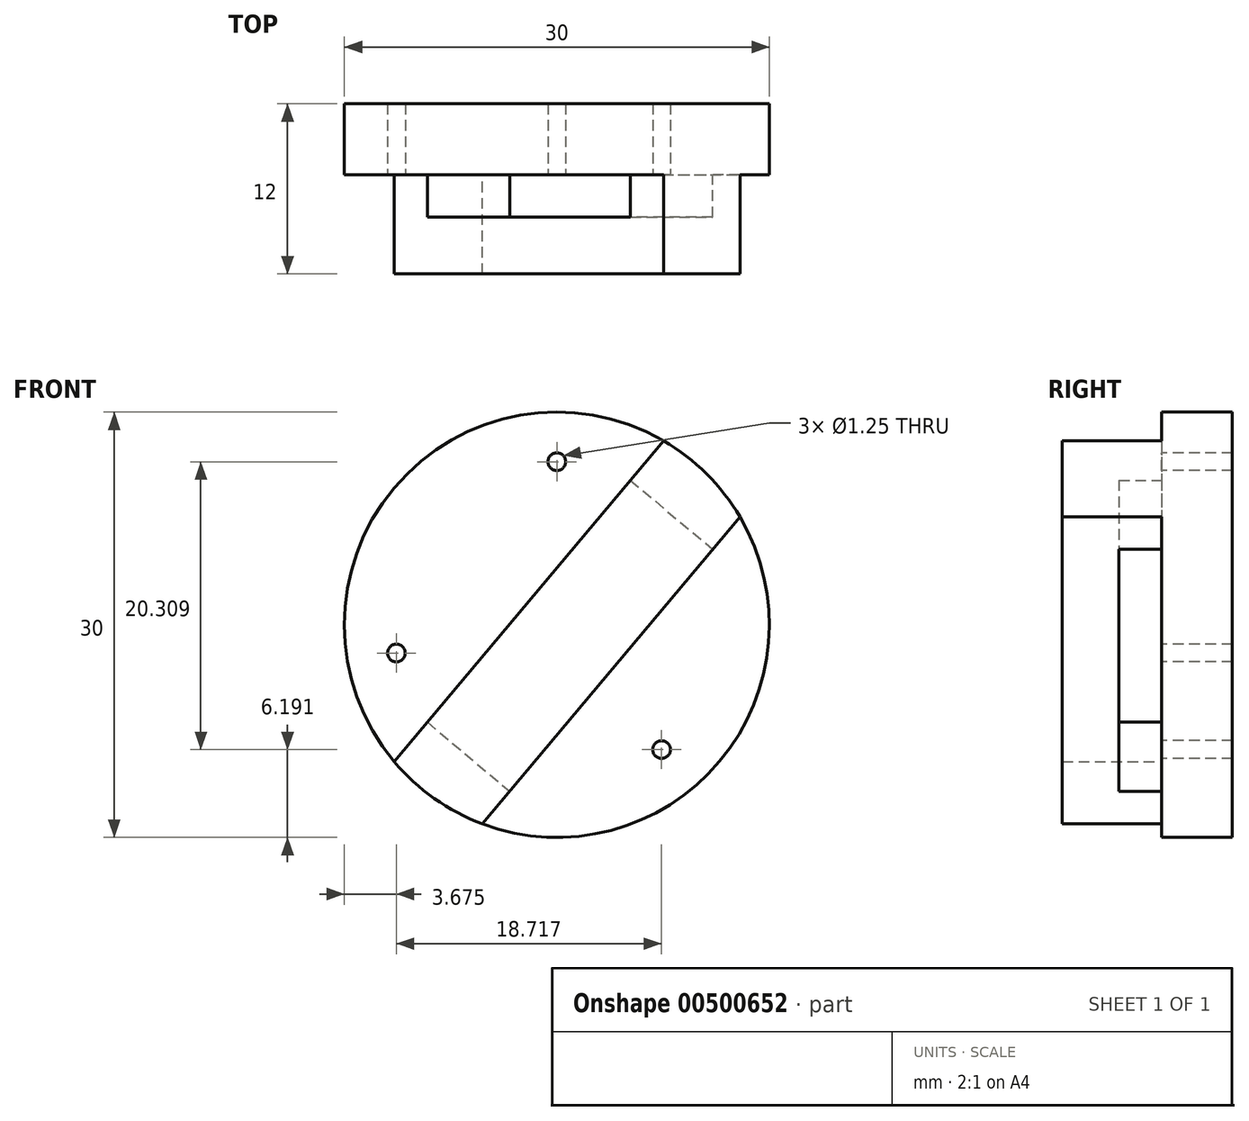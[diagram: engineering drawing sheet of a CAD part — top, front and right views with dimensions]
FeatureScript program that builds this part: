
annotation { "Feature Type Name" : "Feature", "Feature Type Description" : "" }
export const myFeature = defineFeature(function(context is Context, id is Id, definition is map)
    precondition{}
    {
        {
            var Q0;
            Q0=qCreatedBy(makeId("Front.planeOp"),FACE);
            var sketch = newSketch(context, id + "F0", { "sketchPlane" : qUnion([Q0])});
            skCircle(sketch, "E0", {"center": v(0, 0) * mm, "radius": 15 * mm});
            skLineSegment(sketch, "E1", {"start": v(0, 0) * mm, "end": v(0, 15) * mm});
            skLineSegment(sketch, "E2", {"start": v(0, 0) * mm, "end": v(-14.77, -2.6) * mm});
            skLineSegment(sketch, "E3", {"start": v(0, 0) * mm, "end": v(9.64, -11.5) * mm});
            skPoint(sketch, "E4", {"position": v(0, 11.5) * mm});
            skPoint(sketch, "E5", {"position": v(7.4, -8.8) * mm});
            skPoint(sketch, "E6", {"position": v(-11.33, -2) * mm});
            skLineSegment(sketch, "E7", {"start": v(7.53, 12.97) * mm, "end": v(0, 4) * mm});
            skLineSegment(sketch, "E8", {"start": v(0, 4) * mm, "end": v(-3.94, -0.7) * mm});
            skLineSegment(sketch, "E9", {"start": v(-3.94, -0.7) * mm, "end": v(-11.47, -9.67) * mm});
            skLineSegment(sketch, "E10", {"start": v(12.92, 7.62) * mm, "end": v(-5.26, -14.05) * mm});
            skLineSegment(sketch, "E11", {"start": v(5.2, 10.19) * mm, "end": v(11, 5.32) * mm});
            skLineSegment(sketch, "E12", {"start": v(-9.13, -6.88) * mm, "end": v(-3.33, -11.75) * mm});
            skSolve(sketch);
        }
        {
            var Q0;
            {var subQ0=sQuery(id+"F0.wireOp",EDGE,"E7");Q0=makeQuery(id+"F0.imprint","IMPRINT",FACE,{"disambiguationData":[TD([[makeQuery(id+"F0.imprint","IMPRINT",EDGE,{"derivedFrom":subQ0}),1.0]])]});}
            var Q1;
            {var subQ3=sQuery(id+"F0.wireOp",EDGE,"E8");Q1=makeQuery(id+"F0.imprint","IMPRINT",FACE,{"disambiguationData":[TD([[makeQuery(id+"F0.imprint","IMPRINT",EDGE,{"derivedFrom":subQ3}),1.0]])]});}
            var Q2;
            {var subQ0=sQuery(id+"F0.wireOp",EDGE,"E9");Q2=makeQuery(id+"F0.imprint","IMPRINT",FACE,{"disambiguationData":[TD([[makeQuery(id+"F0.imprint","IMPRINT",EDGE,{"derivedFrom":subQ0}),1.0]])]});}
            var Q3;
            {var subQ0=sQuery(id+"F0.wireOp",EDGE,"E12");Q3=makeQuery(id+"F0.imprint","IMPRINT",FACE,{"disambiguationData":[TD([[makeQuery(id+"F0.imprint","IMPRINT",EDGE,{"derivedFrom":subQ0}),1.0]])]});}
            var Q4;
            {var subQ0=sQuery(id+"F0.wireOp",EDGE,"E11");Q4=makeQuery(id+"F0.imprint","IMPRINT",FACE,{"disambiguationData":[TD([[makeQuery(id+"F0.imprint","IMPRINT",EDGE,{"derivedFrom":subQ0}),-1.0]])]});}
            extrude(context, id + "F1", {"entities" : qUnion([Q0, Q1, Q2, Q3, Q4]), "depth" : 12 * mm, "offsetDistance" : 25 * mm});
        }
        {
            var Q0;
            {var subQ3=sQuery(id+"F0.wireOp",EDGE,"E8");Q0=makeQuery(id+"F0.imprint","IMPRINT",FACE,{"disambiguationData":[TD([[makeQuery(id+"F0.imprint","IMPRINT",EDGE,{"derivedFrom":subQ3}),1.0]])]});}
            var Q1;
            {var subQ0=sQuery(id+"F0.wireOp",EDGE,"E11");Q1=makeQuery(id+"F0.imprint","IMPRINT",FACE,{"disambiguationData":[TD([[makeQuery(id+"F0.imprint","IMPRINT",EDGE,{"derivedFrom":subQ0}),-1.0]])]});}
            var Q2;
            {var subQ0=sQuery(id+"F0.wireOp",EDGE,"E12");Q2=makeQuery(id+"F0.imprint","IMPRINT",FACE,{"disambiguationData":[TD([[makeQuery(id+"F0.imprint","IMPRINT",EDGE,{"derivedFrom":subQ0}),1.0]])]});}
            extrude(context, id + "F2", {"entities" : qUnion([Q0, Q1, Q2]), "operationType" : NewBodyOperationType.REMOVE, "depth" : 8 * mm, "offsetDistance" : 25 * mm});
        }
        {
            var Q0;
            {var subQ0=sQuery(id+"F0.wireOp",EDGE,"E1");var subQ1=sQuery(id+"F0.wireOp",EDGE,"E0");var subQ2=makeQuery(id+"F0.imprint","INTERSECT",VERTEX,{"derivedFrom":[subQ1,subQ0]});Q0=makeQuery(id+"F0.imprint","IMPRINT",FACE,{"disambiguationData":[TD([[makeQuery(id+"F0.imprint","IMPRINT",EDGE,{"disambiguationData":[TD([[subQ2,1.0]])],"derivedFrom":subQ1}),1.0]])]});}
            var Q1;
            {var subQ0=sQuery(id+"F0.wireOp",EDGE,"E11");Q1=makeQuery(id+"F0.imprint","IMPRINT",FACE,{"disambiguationData":[TD([[makeQuery(id+"F0.imprint","IMPRINT",EDGE,{"derivedFrom":subQ0}),-1.0]])]});}
            var Q2;
            {var subQ5=sQuery(id+"F0.wireOp",EDGE,"E8");Q2=makeQuery(id+"F0.imprint","IMPRINT",FACE,{"disambiguationData":[TD([[makeQuery(id+"F0.imprint","IMPRINT",EDGE,{"derivedFrom":subQ5}),-1.0]])]});}
            var Q3;
            {var subQ0=sQuery(id+"F0.wireOp",EDGE,"E2");var subQ1=sQuery(id+"F0.wireOp",EDGE,"E0");var subQ2=makeQuery(id+"F0.imprint","INTERSECT",VERTEX,{"derivedFrom":[subQ1,subQ0]});Q3=makeQuery(id+"F0.imprint","IMPRINT",FACE,{"disambiguationData":[TD([[makeQuery(id+"F0.imprint","IMPRINT",EDGE,{"disambiguationData":[TD([[subQ2,-1.0]])],"derivedFrom":subQ1}),1.0]])]});}
            var Q4;
            {var subQ0=sQuery(id+"F0.wireOp",EDGE,"E12");Q4=makeQuery(id+"F0.imprint","IMPRINT",FACE,{"disambiguationData":[TD([[makeQuery(id+"F0.imprint","IMPRINT",EDGE,{"derivedFrom":subQ0}),1.0]])]});}
            var Q5;
            {var subQ3=sQuery(id+"F0.wireOp",EDGE,"E8");Q5=makeQuery(id+"F0.imprint","IMPRINT",FACE,{"disambiguationData":[TD([[makeQuery(id+"F0.imprint","IMPRINT",EDGE,{"derivedFrom":subQ3}),1.0]])]});}
            var Q6;
            {var subQ0=sQuery(id+"F0.wireOp",EDGE,"E3");var subQ1=sQuery(id+"F0.wireOp",EDGE,"E0");var subQ2=makeQuery(id+"F0.imprint","INTERSECT",VERTEX,{"derivedFrom":[subQ1,subQ0]});Q6=makeQuery(id+"F0.imprint","IMPRINT",FACE,{"disambiguationData":[TD([[makeQuery(id+"F0.imprint","IMPRINT",EDGE,{"disambiguationData":[TD([[subQ2,-1.0]])],"derivedFrom":subQ1}),1.0]])]});}
            var Q7;
            {var subQ0=sQuery(id+"F0.wireOp",EDGE,"E3");var subQ1=sQuery(id+"F0.wireOp",EDGE,"E0");var subQ2=makeQuery(id+"F0.imprint","INTERSECT",VERTEX,{"derivedFrom":[subQ1,subQ0]});Q7=makeQuery(id+"F0.imprint","IMPRINT",FACE,{"disambiguationData":[TD([[makeQuery(id+"F0.imprint","IMPRINT",EDGE,{"disambiguationData":[TD([[subQ2,1.0]])],"derivedFrom":subQ1}),1.0]])]});}
            extrude(context, id + "F3", {"entities" : qUnion([Q0, Q1, Q2, Q3, Q4, Q5, Q6, Q7]), "operationType" : NewBodyOperationType.ADD, "offsetDistance" : 25 * mm, "depth" : 5 * mm});
        }
        {
            var Q0;
            Q0=sQuery(id+"F0.wireOp",VERTEX,"E5");
            var Q1;
            Q1=sQuery(id+"F0.wireOp",VERTEX,"E6");
            var Q2;
            Q2=sQuery(id+"F0.wireOp",VERTEX,"E4");
            var Q3;
            Q3=makeQuery(id+"F1.opExtrude","SWEPT_BODY",BODY,{"disambiguationData":[OSD([sQuery(id+"F0.wireOp",EDGE,"E0"),sQuery(id+"F0.wireOp",EDGE,"E7"),sQuery(id+"F0.wireOp",EDGE,"E8"),sQuery(id+"F0.wireOp",EDGE,"E9"),sQuery(id+"F0.wireOp",EDGE,"E10")])]});
            hole(context, id + "F4", {"style" : HoleStyle.SIMPLE, "endStyle" : HoleEndStyle.THROUGH, "oppositeDirection" : true, "holeDiameter" : 1.25 * mm, "majorDiameter" : 5 * mm, "isTappedThrough" : true, "tappedDepth" : 12 * mm, "tapClearance" : 3, "locations" : qUnion([Q0, Q1, Q2]), "scope" : qUnion([Q3]), "startStyle" : HoleStartStyle.SKETCH});
        }
    });
